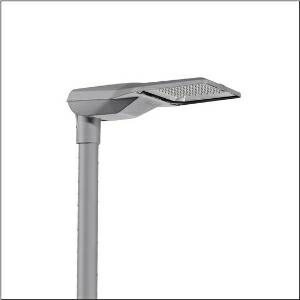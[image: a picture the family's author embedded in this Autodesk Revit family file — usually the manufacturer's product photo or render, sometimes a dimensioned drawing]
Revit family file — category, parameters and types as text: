
# Revit family: streetlight_sl_21_iq_midi___p0_8ab_5xe3r31d08nb_f4a3
name_source: partatom
category: Lighting Fixtures
units: mm (PartAtom-declared; Revit-internal decimal feet)

## family parameters
Cut with Voids When Loaded = No
Host = Face
Light Source = No
Part Type = Normal
Room Calculation Point = No
Round Connector Dimension = Use Diameter
Shared = No

## types (1)
- --- (1 x LED, 20170 lm, 155.5 W, 3000K)
    Apparent Load = 155 VA
    CIE Flux Codes = 39 72 97 100 100
    Color Rendering = 70
    Color Temperature = 3000K
    Default Elevation = 1800 mm
    Description = Streetlight SL 21 iQ midi, mast luminaire, primary light control with lens, of PMMA, primary optical cover: cover, of toughened safety glass, transparent, light distribution: P0.8aB, light emission: direct distribution, primary light characteristic: asymmetric, installation type: post-top, side-entry, LED, High Power LED, rated luminous flux: 20.170lm, luminous efficacy: 130lm/W, light colour: 730, colour temperature: 3000K, control gear: iQ-Comfort, control: pre-setting: linear dimming characteristic, Auto-Match, Temp-Guard, Lumen-Switch, Night-Set, Smart-Wire, Light-Fading, Desk-Remote (wireless, voltage-free reading and setting of iQ features in the workshop via application-optimized NFC function/RFID function), optimised constant luminous flux control (CLO 2.0), mains connection: 230..240V, AC, 50/60Hz, start of lifetime: 156W, end of service life: 162W, reduction: 69W, luminaire housing, of diecast aluminium, powder-coated, Siteco® metallic grey (DB 702S), corrosivity category C5 mid according to DIN EN ISO 12944, please order mast flange separately, inclination adjustable: 0°, 5°, 10°, 15°, sealing non-destructively replaceable, multi-level sealing system, length: 644mm, width: 335mm, height: 110mm, mast flange for spigot size: 42mm (side-entry): 5XC10008XM4, 60/48mm (side-entry/post-top): 5XC10108XM2, 76/60mm (side-entry/post-top): 5XC10108XM1, mounting height: 4..8m, protection rating (complete): IP66, insulation class (complete): insulation class II (safety insulation), certification: CE, ENEC, ENEC+, VDE, impact resistance: IK10, permissible operating ambient temperature for outdoor applications: -40..+50°C, standard-compliant lighting for roads and squares, packaging unit: 1 piece

Light Distribution: P0.8aB
    Height = 111 mm
    Lamp = 1 x LED
    Lamp Light Flux = 20170 lm
    Lamp Power = 155.5 W
    Lamp count = 1
    Length = 644 mm
    Luminous efficacy = 130 lm/W
    Manufacturer = Siteco
    ModVariant = No
    Model = 5XE3R31D08NB
    Number of Poles = 1
    OnlyDefault = Yes
    Power Factor = 1
    Product Name = Streetlight SL 21 iQ midi | P0.8aB
    Product group = mast luminaire | pylon top
    ProductGroupID = 6100
    Protection Class = Protection class II
    Protection Degree = IP 66
    RLX_Detail_Level = 1
    RLX_Emergency_Light_Flux = 0 lm
    RLX_Emergency_Type = 0
    RLX_Emergency_Type_DB = No
    RlxData = <blob elided: 90677 chars, md5=f1c5c0a1>
    Socket = socket
    Standby Power = 0 W
    System Light Flux = 20170 lm
    System Power = 155 W
    Type Comments = factory setting: luminous flux: 100 % | dim-lin: 254 | 823 mA
    Type Image = l_1004298.jpg
    URL = http://relux.com
    VarID = @adj_092581
    Voltage = 0 V
    Weight = 0.00 kg
    Width = 336 mm

## geometry (parser evidence)
native form markers: Blend x4, Sweep x11
no freeform markers — native parametric forms only
